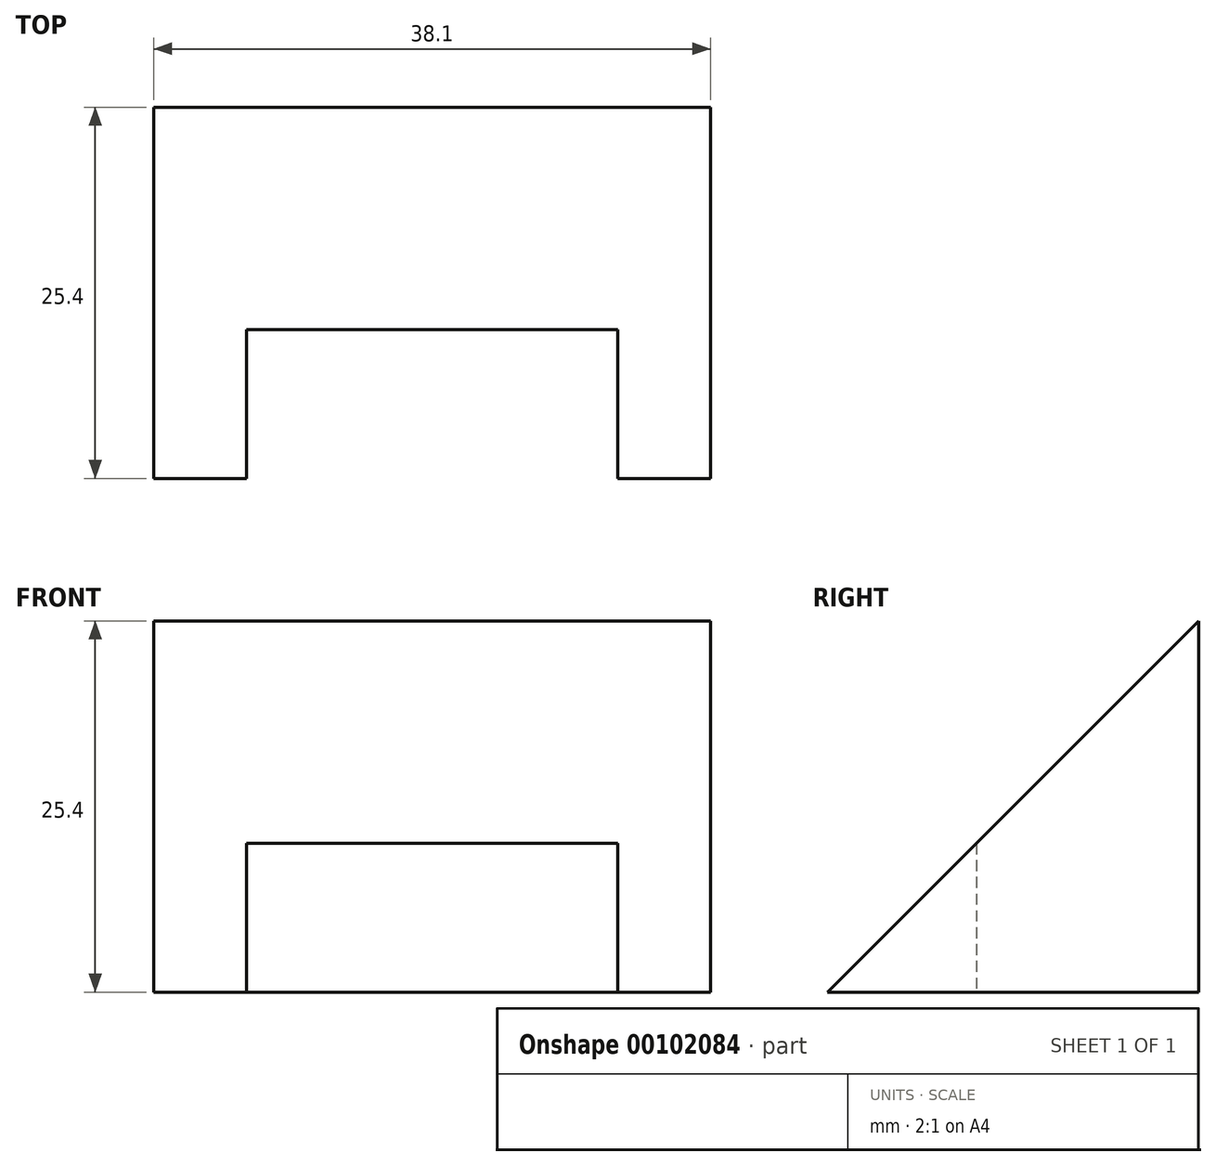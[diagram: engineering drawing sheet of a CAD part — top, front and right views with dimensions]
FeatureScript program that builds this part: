
annotation { "Feature Type Name" : "Feature", "Feature Type Description" : "" }
export const myFeature = defineFeature(function(context is Context, id is Id, definition is map)
    precondition{}
    {
        {
            var Q0;
            Q0=qCreatedBy(makeId("Right.planeOp"),FACE);
            var sketch = newSketch(context, id + "F0", { "sketchPlane" : qUnion([Q0])});
            skLineSegment(sketch, "E0", {"start": v(0, 0) * mm, "end": v(0, 25.4) * mm});
            skLineSegment(sketch, "E1", {"start": v(0, 25.4) * mm, "end": v(-25.4, 0) * mm});
            skLineSegment(sketch, "E2", {"start": v(-25.4, 0) * mm, "end": v(0, 0) * mm});
            skSolve(sketch);
        }
        {
            var Q0;
            Q0 = qSketchRegion(id + "F0", true);
            extrude(context, id + "F1", {"entities" : qUnion([Q0]), "endBound" : BoundingType.SYMMETRIC, "depth" : 38.1 * mm});
        }
        {
            var Q0;
            Q0=qCreatedBy(makeId("Right.planeOp"),FACE);
            var sketch = newSketch(context, id + "F2", { "sketchPlane" : qUnion([Q0])});
            skLineSegment(sketch, "E3", {"start": v(0, 0) * mm, "end": v(0, 0) * mm});
            skLineSegment(sketch, "E4", {"start": v(-15.22, 10.21) * mm, "end": v(-15.22, 0) * mm});
            skLineSegment(sketch, "E5", {"start": v(-15.22, 0) * mm, "end": v(-25.42, 0) * mm});
            skLineSegment(sketch, "E6", {"start": v(-25.42, 0) * mm, "end": v(-15.22, 10.21) * mm});
            skSolve(sketch);
        }
        {
            var Q0;
            Q0 = qSketchRegion(id + "F2", true);
            extrude(context, id + "F3", {"entities" : qUnion([Q0]), "operationType" : NewBodyOperationType.REMOVE, "endBound" : BoundingType.SYMMETRIC, "oppositeDirection" : true, "depth" : 25.4 * mm});
        }
    });
